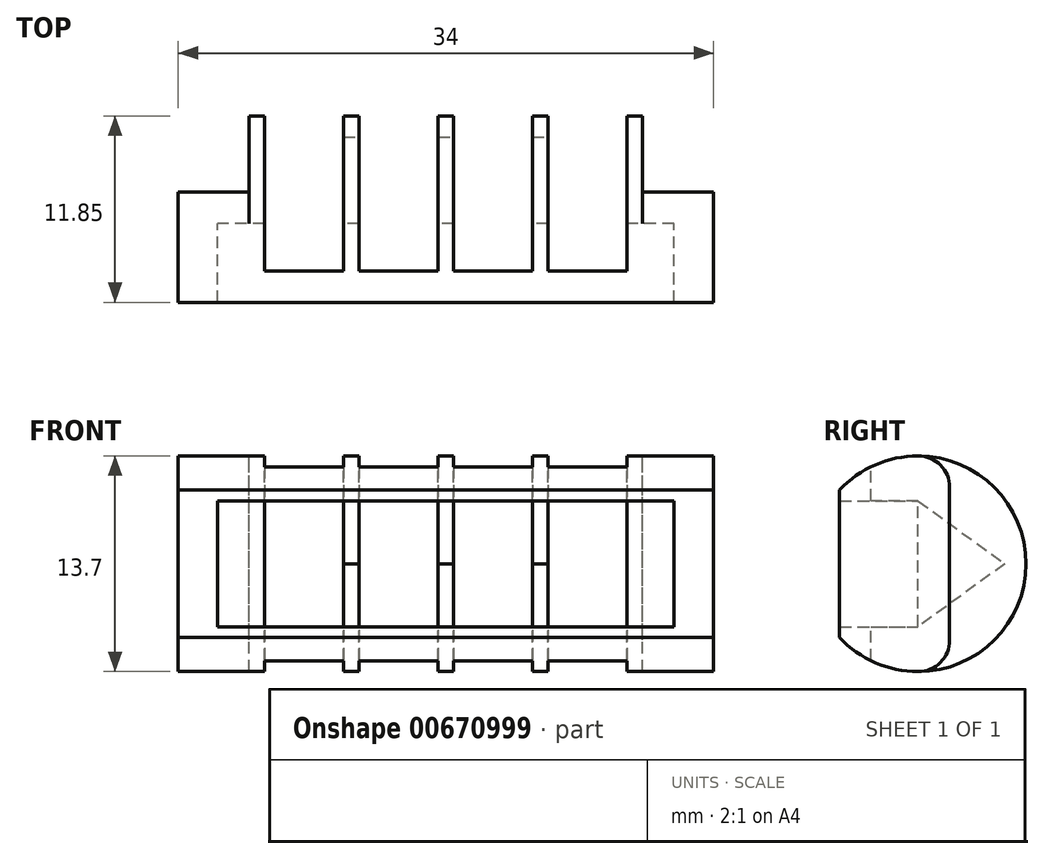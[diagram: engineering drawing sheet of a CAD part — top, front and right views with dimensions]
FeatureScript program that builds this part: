
annotation { "Feature Type Name" : "Feature", "Feature Type Description" : "" }
export const myFeature = defineFeature(function(context is Context, id is Id, definition is map)
    precondition{}
    {
        {
            var Q0;
            Q0=qCreatedBy(makeId("Right.planeOp"),FACE);
            var sketch = newSketch(context, id + "F0", { "sketchPlane" : qUnion([Q0])});
            skArc(sketch, "E0", {"start": v(-5, 4.68) * mm, "mid": v(6.85, 0) * mm, "end": v(-5, -4.68) * mm});
            skLineSegment(sketch, "E1", {"start": v(-5, 4.68) * mm, "end": v(-5, 4) * mm});
            skLineSegment(sketch, "E2", {"start": v(-5, 4) * mm, "end": v(0, 4) * mm});
            skLineSegment(sketch, "E3", {"start": v(0, 4) * mm, "end": v(0, -4) * mm});
            skLineSegment(sketch, "E4", {"start": v(0, -4) * mm, "end": v(-5, -4) * mm});
            skLineSegment(sketch, "E5", {"start": v(-5, -4) * mm, "end": v(-5, -4.68) * mm});
            skSolve(sketch);
        }
        {
            var Q0;
            Q0 = qSketchRegion(id + "F0", true);
            extrude(context, id + "F1", {"entities" : qUnion([Q0]), "depth" : 17 * mm, "offsetDistance" : 25 * mm, "hasSecondDirection" : true, "secondDirectionOppositeDirection" : true, "secondDirectionDepth" : 17 * mm});
        }
        {
            var Q0;
            Q0=qCreatedBy(makeId("Top.planeOp"),FACE);
            var sketch = newSketch(context, id + "F2", { "sketchPlane" : qUnion([Q0])});
            skLineSegment(sketch, "E6.bottom", {"start": v(-11.5, 14) * mm, "end": v(-6.5, 14) * mm});
            skLineSegment(sketch, "E6.top", {"start": v(-11.5, -3) * mm, "end": v(-6.5, -3) * mm});
            skLineSegment(sketch, "E6.left", {"start": v(-11.5, 14) * mm, "end": v(-11.5, -3) * mm});
            skLineSegment(sketch, "E6.right", {"start": v(-6.5, 14) * mm, "end": v(-6.5, -3) * mm});
            skLineSegment(sketch, "E7.bottom", {"start": v(-5.5, 14) * mm, "end": v(-0.5, 14) * mm});
            skLineSegment(sketch, "E7.top", {"start": v(-5.5, -3) * mm, "end": v(-0.5, -3) * mm});
            skLineSegment(sketch, "E7.left", {"start": v(-5.5, 14) * mm, "end": v(-5.5, -3) * mm});
            skLineSegment(sketch, "E7.right", {"start": v(-0.5, 14) * mm, "end": v(-0.5, -3) * mm});
            skLineSegment(sketch, "E8.MirrorCS", {"start": v(5.5, 14) * mm, "end": v(0.5, 14) * mm});
            skLineSegment(sketch, "E9.MirrorCS", {"start": v(6.5, 14) * mm, "end": v(6.5, -3) * mm});
            skLineSegment(sketch, "E10.MirrorCS", {"start": v(11.5, 14) * mm, "end": v(11.5, -3) * mm});
            skLineSegment(sketch, "E11.MirrorCS", {"start": v(11.5, -3) * mm, "end": v(6.5, -3) * mm});
            skLineSegment(sketch, "E12.MirrorCS", {"start": v(0.5, 14) * mm, "end": v(0.5, -3) * mm});
            skLineSegment(sketch, "E13.MirrorCS", {"start": v(5.5, 14) * mm, "end": v(5.5, -3) * mm});
            skLineSegment(sketch, "E14.MirrorCS", {"start": v(5.5, -3) * mm, "end": v(0.5, -3) * mm});
            skLineSegment(sketch, "E15.MirrorCS", {"start": v(11.5, 14) * mm, "end": v(6.5, 14) * mm});
            skSolve(sketch);
        }
        {
            var Q0;
            Q0 = qSketchRegion(id + "F2", true);
            extrude(context, id + "F3", {"entities" : qUnion([Q0]), "operationType" : NewBodyOperationType.REMOVE, "oppositeDirection" : true, "depth" : 25 * mm, "offsetDistance" : 25 * mm, "hasSecondDirection" : true, "secondDirectionOppositeDirection" : false, "secondDirectionDepth" : 25 * mm});
        }
        {
            var Q0;
            Q0=qCreatedBy(makeId("Right.planeOp"),FACE);
            var sketch = newSketch(context, id + "F4", { "sketchPlane" : qUnion([Q0])});
            skCircle(sketch, "E16", {"center": v(0, 0) * mm, "radius": 5.5 * mm, "construction": true});
            skLineSegment(sketch, "E17", {"start": v(5.5, 0) * mm, "end": v(0, 4) * mm});
            skLineSegment(sketch, "E18", {"start": v(0, -4) * mm, "end": v(5.5, 0) * mm});
            skLineSegment(sketch, "E19", {"start": v(0, 4) * mm, "end": v(0, -4) * mm});
            skSolve(sketch);
        }
        {
            var Q0;
            Q0 = qSketchRegion(id + "F4", true);
            extrude(context, id + "F5", {"entities" : qUnion([Q0]), "operationType" : NewBodyOperationType.REMOVE, "oppositeDirection" : true, "depth" : 10 * mm, "offsetDistance" : 25 * mm, "hasSecondDirection" : true, "secondDirectionOppositeDirection" : false, "secondDirectionDepth" : 10 * mm});
        }
        {
            var Q0;
            {var subQ1=sQuery(id+"F0.wireOp",EDGE,"E3");Q0=makeQuery(id+"F3.boolean.opBoolean","SPLIT",FACE,{"disambiguationData":[TD([makeQuery(id+"F3.opExtrude","SWEPT_FACE",FACE,{"disambiguationData":[OSD([sQuery(id+"F2.wireOp",EDGE,"E6.left")])]})])],"derivedFrom":makeQuery(id+"F1.opExtrude","SWEPT_FACE",FACE,{"disambiguationData":[OSD([subQ1])]})});}
            var sketch = newSketch(context, id + "F6", { "sketchPlane" : qUnion([Q0])});
            skLineSegment(sketch, "E20.bottom", {"start": v(17, -4) * mm, "end": v(14.5, -4) * mm});
            skLineSegment(sketch, "E20.top", {"start": v(17, 4) * mm, "end": v(14.5, 4) * mm});
            skLineSegment(sketch, "E20.left", {"start": v(17, -4) * mm, "end": v(17, 4) * mm});
            skLineSegment(sketch, "E20.right", {"start": v(14.5, -4) * mm, "end": v(14.5, 4) * mm});
            skLineSegment(sketch, "E21.bottom", {"start": v(-17, -4) * mm, "end": v(-14.5, -4) * mm});
            skLineSegment(sketch, "E21.top", {"start": v(-17, 4) * mm, "end": v(-14.5, 4) * mm});
            skLineSegment(sketch, "E21.left", {"start": v(-17, -4) * mm, "end": v(-17, 4) * mm});
            skLineSegment(sketch, "E21.right", {"start": v(-14.5, -4) * mm, "end": v(-14.5, 4) * mm});
            skSolve(sketch);
        }
        {
            var Q0;
            Q0 = qSketchRegion(id + "F6", true);
            var Q1;
            Q1=makeQuery(id+"F1.opExtrude","SWEPT_FACE",FACE,{"disambiguationData":[OSD([sQuery(id+"F0.wireOp",EDGE,"E5")])]});
            extrude(context, id + "F7", {"entities" : qUnion([Q0]), "operationType" : NewBodyOperationType.ADD, "endBound" : BoundingType.UP_TO_SURFACE, "depth" : 25 * mm, "endBoundEntityFace" : qUnion([Q1]), "offsetDistance" : 25 * mm});
        }
        {
            var Q0;
            Q0=qCreatedBy(makeId("Top.planeOp"),FACE);
            var sketch = newSketch(context, id + "F8", { "sketchPlane" : qUnion([Q0])});
            skLineSegment(sketch, "E22.bottom", {"start": v(-17, 2) * mm, "end": v(-12.5, 2) * mm});
            skLineSegment(sketch, "E22.top", {"start": v(-17, 9) * mm, "end": v(-12.5, 9) * mm});
            skLineSegment(sketch, "E22.left", {"start": v(-17, 2) * mm, "end": v(-17, 9) * mm});
            skLineSegment(sketch, "E22.right", {"start": v(-12.5, 2) * mm, "end": v(-12.5, 9) * mm});
            skLineSegment(sketch, "E23.bottom", {"start": v(17, 2) * mm, "end": v(12.5, 2) * mm});
            skLineSegment(sketch, "E23.top", {"start": v(17, 9) * mm, "end": v(12.5, 9) * mm});
            skLineSegment(sketch, "E23.left", {"start": v(17, 2) * mm, "end": v(17, 9) * mm});
            skLineSegment(sketch, "E23.right", {"start": v(12.5, 2) * mm, "end": v(12.5, 9) * mm});
            skSolve(sketch);
        }
        {
            var Q0;
            Q0=makeQuery(id+"F8.imprint","IMPRINT",FACE,{"disambiguationData":[TD([[makeQuery(id+"F8.imprint","IMPRINT",EDGE,{"derivedFrom":sQuery(id+"F8.wireOp",EDGE,"E22.bottom")}),1.0]])]});
            var Q1;
            Q1=makeQuery(id+"F8.imprint","IMPRINT",FACE,{"disambiguationData":[TD([[makeQuery(id+"F8.imprint","IMPRINT",EDGE,{"derivedFrom":sQuery(id+"F8.wireOp",EDGE,"E23.bottom")}),-1.0]])]});
            extrude(context, id + "F9", {"entities" : qUnion([Q0, Q1]), "operationType" : NewBodyOperationType.REMOVE, "oppositeDirection" : true, "depth" : 25 * mm, "offsetDistance" : 25 * mm, "hasSecondDirection" : true, "secondDirectionOppositeDirection" : false, "secondDirectionDepth" : 25 * mm});
        }
        {
            var Q0;
            Q0=makeQuery(id+"F9.boolean.opBoolean","COPY",EDGE,{"derivedFrom":makeQuery(id+"F9.opExtrude","SWEPT_EDGE",EDGE,{"disambiguationData":[OSD([sQuery(id+"F8.wireOp",EDGE,"E23.bottom"),sQuery(id+"F8.wireOp",EDGE,"E23.left")])]})});
            var Q1;
            Q1=makeQuery(id+"F9.boolean.opBoolean","COPY",EDGE,{"derivedFrom":makeQuery(id+"F9.opExtrude","SWEPT_EDGE",EDGE,{"disambiguationData":[OSD([sQuery(id+"F8.wireOp",EDGE,"E22.bottom"),sQuery(id+"F8.wireOp",EDGE,"E22.left")])]})});
            var Q2;
            Q2=makeQuery(id+"F9.boolean.opBoolean","INTERSECT",EDGE,{"disambiguationData":[OD(1.0)],"derivedFrom":[makeQuery(id+"F1.opExtrude","SWEPT_FACE",FACE,{"disambiguationData":[OSD([sQuery(id+"F0.wireOp",EDGE,"E0")])]}),makeQuery(id+"F9.opExtrude","SWEPT_FACE",FACE,{"disambiguationData":[OSD([sQuery(id+"F8.wireOp",EDGE,"E23.bottom")])]})]});
            var Q3;
            Q3=makeQuery(id+"F9.boolean.opBoolean","INTERSECT",EDGE,{"disambiguationData":[OD(0.0)],"derivedFrom":[makeQuery(id+"F1.opExtrude","SWEPT_FACE",FACE,{"disambiguationData":[OSD([sQuery(id+"F0.wireOp",EDGE,"E0")])]}),makeQuery(id+"F9.opExtrude","SWEPT_FACE",FACE,{"disambiguationData":[OSD([sQuery(id+"F8.wireOp",EDGE,"E23.bottom")])]})]});
            var Q4;
            Q4=makeQuery(id+"F9.boolean.opBoolean","INTERSECT",EDGE,{"disambiguationData":[OD(1.0)],"derivedFrom":[makeQuery(id+"F1.opExtrude","SWEPT_FACE",FACE,{"disambiguationData":[OSD([sQuery(id+"F0.wireOp",EDGE,"E0")])]}),makeQuery(id+"F9.opExtrude","SWEPT_FACE",FACE,{"disambiguationData":[OSD([sQuery(id+"F8.wireOp",EDGE,"E22.bottom")])]})]});
            var Q5;
            Q5=makeQuery(id+"F9.boolean.opBoolean","INTERSECT",EDGE,{"disambiguationData":[OD(0.0)],"derivedFrom":[makeQuery(id+"F1.opExtrude","SWEPT_FACE",FACE,{"disambiguationData":[OSD([sQuery(id+"F0.wireOp",EDGE,"E0")])]}),makeQuery(id+"F9.opExtrude","SWEPT_FACE",FACE,{"disambiguationData":[OSD([sQuery(id+"F8.wireOp",EDGE,"E22.bottom")])]})]});
            fillet(context, id + "F10", {"entities" : qUnion([Q0, Q1, Q2, Q3, Q4, Q5]), "radius" : 2 * mm, "tangentPropagation" : true, "allowEdgeOverflow" : false});
        }
    });
